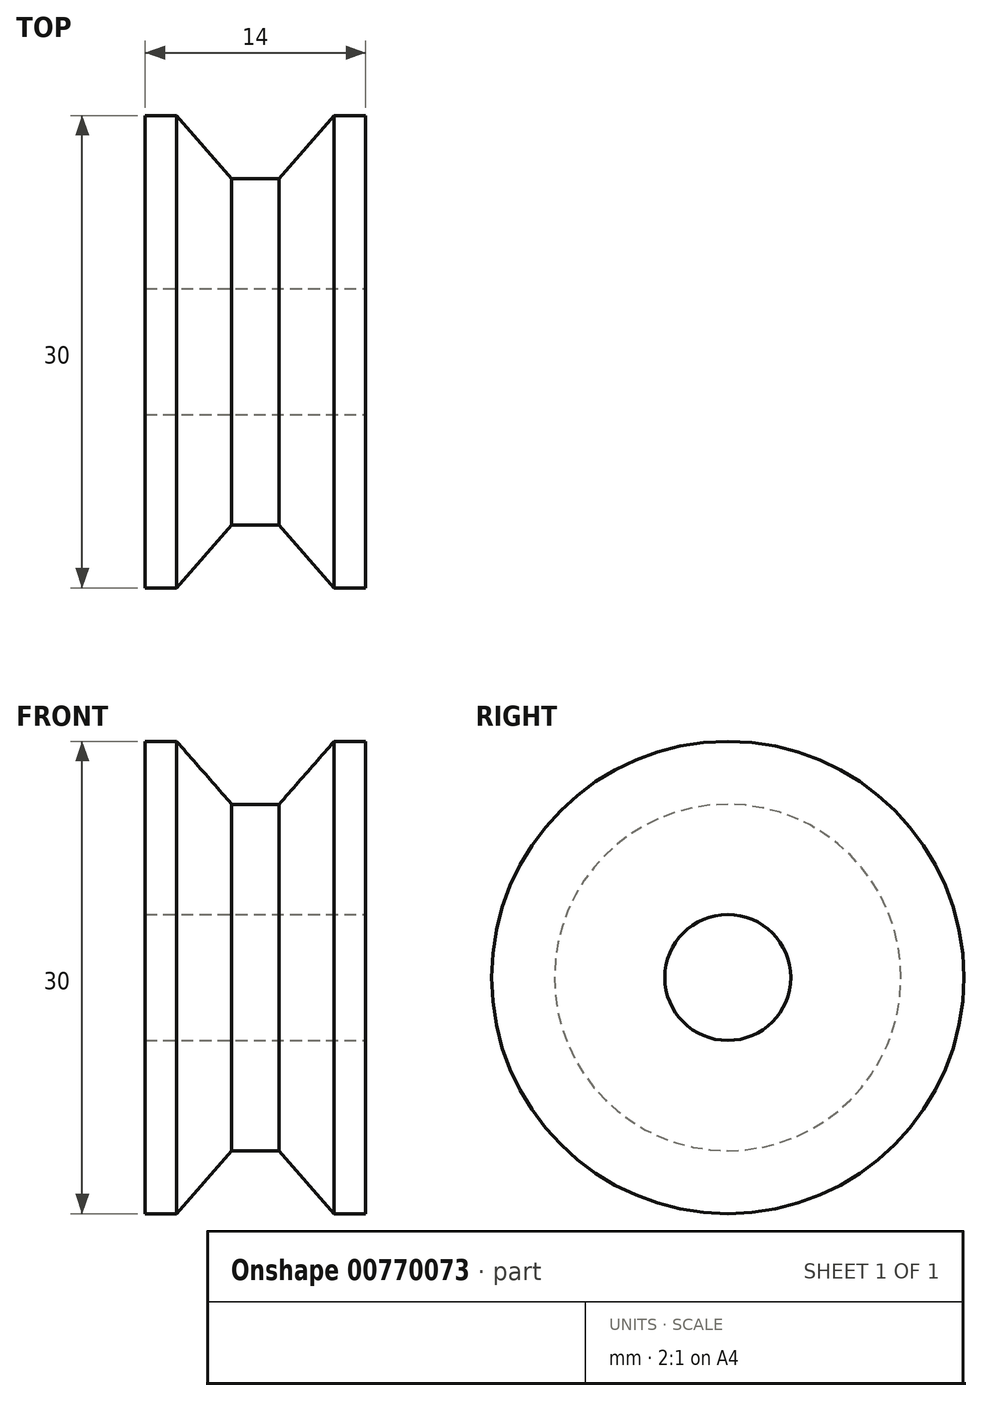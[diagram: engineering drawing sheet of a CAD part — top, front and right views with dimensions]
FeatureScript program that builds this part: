
annotation { "Feature Type Name" : "Feature", "Feature Type Description" : "" }
export const myFeature = defineFeature(function(context is Context, id is Id, definition is map)
    precondition{}
    {
        {
            var Q0;
            Q0=qCreatedBy(makeId("Front.planeOp"),FACE);
            var sketch = newSketch(context, id + "F0", { "sketchPlane" : qUnion([Q0])});
            skLineSegment(sketch, "E0", {"start": v(0, 0) * mm, "end": v(-7, 0) * mm});
            skLineSegment(sketch, "E1", {"start": v(-7, 0) * mm, "end": v(-7, 15) * mm});
            skLineSegment(sketch, "E2", {"start": v(-7, 15) * mm, "end": v(-5, 15) * mm});
            skLineSegment(sketch, "E3", {"start": v(-5, 15) * mm, "end": v(-1.5, 11) * mm});
            skLineSegment(sketch, "E4", {"start": v(-1.5, 11) * mm, "end": v(0, 11) * mm});
            skLineSegment(sketch, "E5", {"start": v(0, 11) * mm, "end": v(0, 0) * mm});
            skLineSegment(sketch, "E6.MirrorCS", {"start": v(0, 0) * mm, "end": v(7, 0) * mm});
            skLineSegment(sketch, "E7.MirrorCS", {"start": v(7, 0) * mm, "end": v(7, 15) * mm});
            skLineSegment(sketch, "E8.MirrorCS", {"start": v(7, 15) * mm, "end": v(5, 15) * mm});
            skLineSegment(sketch, "E9.MirrorCS", {"start": v(5, 15) * mm, "end": v(1.5, 11) * mm});
            skLineSegment(sketch, "E10.MirrorCS", {"start": v(1.5, 11) * mm, "end": v(0, 11) * mm});
            skSolve(sketch);
        }
        {
            var Q0;
            Q0=qCreatedBy(makeId("Right.planeOp"),FACE);
            var sketch = newSketch(context, id + "F1", { "sketchPlane" : qUnion([Q0])});
            skCircle(sketch, "E11", {"center": v(0, 0) * mm, "radius": 4 * mm});
            skSolve(sketch);
        }
        {
            var Q0;
            Q0=makeQuery(id+"F0.imprint","IMPRINT",FACE,{"disambiguationData":[TD([[makeQuery(id+"F0.imprint","IMPRINT",EDGE,{"derivedFrom":sQuery(id+"F0.wireOp",EDGE,"E5")}),1.0]])]});
            var Q1;
            Q1=makeQuery(id+"F0.imprint","IMPRINT",FACE,{"disambiguationData":[TD([[makeQuery(id+"F0.imprint","IMPRINT",EDGE,{"derivedFrom":sQuery(id+"F0.wireOp",EDGE,"E0")}),-1.0]])]});
            var Q2;
            Q2=sQuery(id+"F1.wireOp",EDGE,"E11");
            revolve(context, id + "F2", {"surfaceOperationType" : NewSurfaceOperationType.NEW, "entities" : qUnion([Q0, Q1]), "axis" : qUnion([Q2]), "revolveType" : RevolveType.FULL});
        }
        {
            var Q0;
            Q0 = qSketchRegion(id + "F1", true);
            extrude(context, id + "F3", {"entities" : qUnion([Q0]), "operationType" : NewBodyOperationType.REMOVE, "endBound" : BoundingType.SYMMETRIC, "oppositeDirection" : true, "depth" : 25 * mm, "offsetDistance" : 25 * mm});
        }
    });
